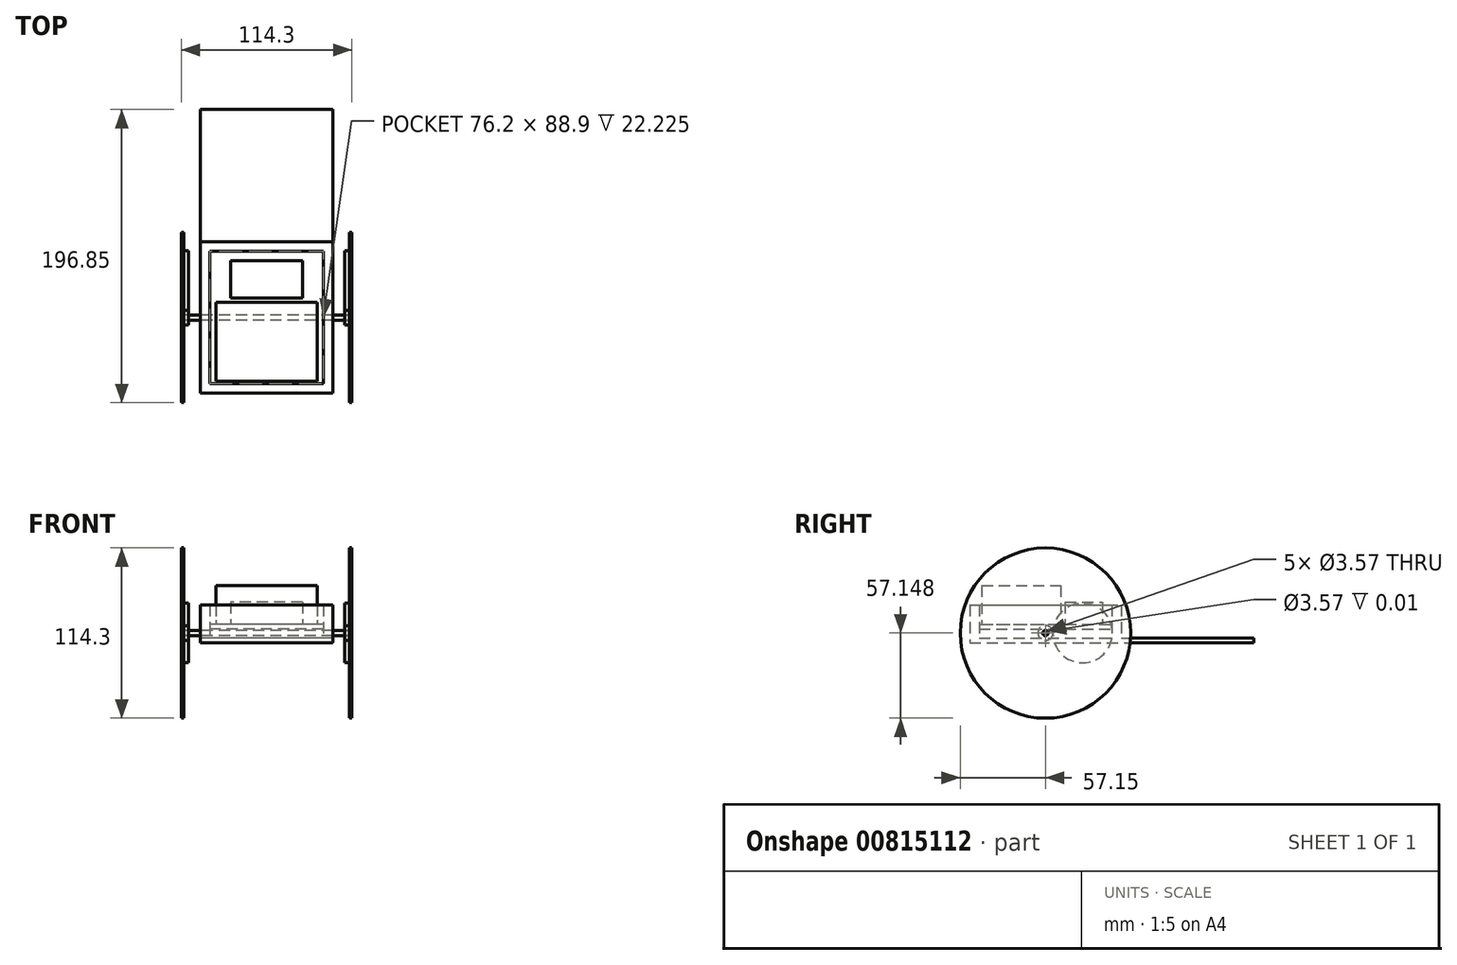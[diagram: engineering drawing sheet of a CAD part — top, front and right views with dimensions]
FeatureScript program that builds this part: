
annotation { "Feature Type Name" : "Feature", "Feature Type Description" : "" }
export const myFeature = defineFeature(function(context is Context, id is Id, definition is map)
    precondition{}
    {
        {
            var Q0;
            Q0=qCreatedBy(makeId("Top.planeOp"),FACE);
            var sketch = newSketch(context, id + "F0", { "sketchPlane" : qUnion([Q0])});
            skLineSegment(sketch, "E0.bottom", {"start": v(44.45, -50.8) * mm, "end": v(-44.45, -50.8) * mm});
            skLineSegment(sketch, "E0.top", {"start": v(44.45, 50.8) * mm, "end": v(-44.45, 50.8) * mm});
            skLineSegment(sketch, "E0.left", {"start": v(44.45, -50.8) * mm, "end": v(44.45, 50.8) * mm});
            skLineSegment(sketch, "E0.right", {"start": v(-44.45, -50.8) * mm, "end": v(-44.45, 50.8) * mm});
            skPoint(sketch, "E0.middle", {"position": v(0, 0) * mm});
            skLineSegment(sketch, "E1.bottom", {"start": v(38.1, -44.45) * mm, "end": v(-38.1, -44.45) * mm});
            skLineSegment(sketch, "E1.top", {"start": v(38.1, 44.45) * mm, "end": v(-38.1, 44.45) * mm});
            skLineSegment(sketch, "E1.left", {"start": v(38.1, -44.45) * mm, "end": v(38.1, 44.45) * mm});
            skLineSegment(sketch, "E1.right", {"start": v(-38.1, -44.45) * mm, "end": v(-38.1, 44.45) * mm});
            skLineSegment(sketch, "E2.top", {"start": v(-44.45, 139.7) * mm, "end": v(44.45, 139.7) * mm});
            skLineSegment(sketch, "E2.left", {"start": v(-44.45, 50.8) * mm, "end": v(-44.45, 139.7) * mm});
            skLineSegment(sketch, "E2.right", {"start": v(44.45, 50.8) * mm, "end": v(44.45, 139.7) * mm});
            skSolve(sketch);
        }
        {
            var Q0;
            Q0=makeQuery(id+"F0.imprint","IMPRINT",FACE,{"disambiguationData":[TD([[makeQuery(id+"F0.imprint","IMPRINT",EDGE,{"derivedFrom":sQuery(id+"F0.wireOp",EDGE,"E0.bottom")}),-1.0]])]});
            extrude(context, id + "F1", {"entities" : qUnion([Q0]), "depth" : 25.4 * mm, "offsetDistance" : 25.4 * mm});
        }
        {
            var Q0;
            Q0=makeQuery(id+"F0.imprint","IMPRINT",FACE,{"disambiguationData":[TD([[makeQuery(id+"F0.imprint","IMPRINT",EDGE,{"derivedFrom":sQuery(id+"F0.wireOp",EDGE,"E1.bottom")}),-1.0]])]});
            extrude(context, id + "F2", {"entities" : qUnion([Q0]), "operationType" : NewBodyOperationType.ADD, "depth" : 3.17 * mm, "offsetDistance" : 25.4 * mm});
        }
        {
            var Q0;
            Q0=makeQuery(id+"F1.opExtrude","SWEPT_FACE",FACE,{"disambiguationData":[OSD([sQuery(id+"F0.wireOp",EDGE,"E1.right")])]});
            var sketch = newSketch(context, id + "F3", { "sketchPlane" : qUnion([Q0])});
            skLineSegment(sketch, "E3.bottom", {"start": v(-44.45, 12.3) * mm, "end": v(44.45, 12.3) * mm});
            skLineSegment(sketch, "E3.top", {"start": v(-44.45, 9.13) * mm, "end": v(44.45, 9.13) * mm});
            skLineSegment(sketch, "E3.left", {"start": v(-44.45, 12.3) * mm, "end": v(-44.45, 9.13) * mm});
            skLineSegment(sketch, "E3.right", {"start": v(44.45, 12.3) * mm, "end": v(44.45, 9.13) * mm});
            skSolve(sketch);
        }
        {
            var Q0;
            Q0=makeQuery(id+"F3.imprint","IMPRINT",FACE,{"disambiguationData":[TD([[makeQuery(id+"F3.imprint","IMPRINT",EDGE,{"derivedFrom":sQuery(id+"F3.wireOp",EDGE,"E3.bottom")}),-1.0]])]});
            extrude(context, id + "F4", {"entities" : qUnion([Q0]), "depth" : 76.2 * mm, "offsetDistance" : 25.4 * mm});
        }
        {
            var Q0;
            Q0=makeQuery(id+"F4.opExtrude","SWEPT_FACE",FACE,{"disambiguationData":[OSD([sQuery(id+"F3.wireOp",EDGE,"E3.bottom")])]});
            var sketch = newSketch(context, id + "F5", { "sketchPlane" : qUnion([Q0])});
            skLineSegment(sketch, "E4.bottom", {"start": v(24, 13.2) * mm, "end": v(-24, 13.2) * mm});
            skLineSegment(sketch, "E4.top", {"start": v(24, 38.2) * mm, "end": v(-24, 38.2) * mm});
            skLineSegment(sketch, "E4.left", {"start": v(24, 13.2) * mm, "end": v(24, 38.2) * mm});
            skLineSegment(sketch, "E4.right", {"start": v(-24, 13.2) * mm, "end": v(-24, 38.2) * mm});
            skPoint(sketch, "E4.middle", {"position": v(0, 25.7) * mm});
            skLineSegment(sketch, "E5.bottom", {"start": v(34, -42.7) * mm, "end": v(-34, -42.7) * mm});
            skLineSegment(sketch, "E5.top", {"start": v(34, 10.3) * mm, "end": v(-34, 10.3) * mm});
            skLineSegment(sketch, "E5.left", {"start": v(34, -42.7) * mm, "end": v(34, 10.3) * mm});
            skLineSegment(sketch, "E5.right", {"start": v(-34, -42.7) * mm, "end": v(-34, 10.3) * mm});
            skPoint(sketch, "E5.middle", {"position": v(0, -16.2) * mm});
            skSolve(sketch);
        }
        {
            var Q0;
            Q0=makeQuery(id+"F5.imprint","IMPRINT",FACE,{"disambiguationData":[TD([[makeQuery(id+"F5.imprint","IMPRINT",EDGE,{"derivedFrom":sQuery(id+"F5.wireOp",EDGE,"E4.bottom")}),-1.0]])]});
            extrude(context, id + "F6", {"entities" : qUnion([Q0]), "depth" : 15 * mm, "offsetDistance" : 25.4 * mm});
        }
        {
            var Q0;
            {var subQ0=sQuery(id+"F5.wireOp",EDGE,"E5.top");Q0=makeQuery(id+"F5.imprint","IMPRINT",FACE,{"disambiguationData":[TD([[makeQuery(id+"F5.imprint","IMPRINT",EDGE,{"derivedFrom":subQ0}),1.0]])]});}
            extrude(context, id + "F7", {"entities" : qUnion([Q0]), "depth" : 26 * mm, "offsetDistance" : 25.4 * mm});
        }
        {
            var Q0;
            Q0=makeQuery(id+"F1.opExtrude","SWEPT_FACE",FACE,{"disambiguationData":[OSD([sQuery(id+"F0.wireOp",EDGE,"E0.right")])]});
            var sketch = newSketch(context, id + "F8", { "sketchPlane" : qUnion([Q0])});
            skLineSegment(sketch, "E6", {"start": v(0, 0) * mm, "end": v(0, 25.4) * mm, "construction": true});
            skCircle(sketch, "E7", {"center": v(0, 6.55) * mm, "radius": 1.79 * mm});
            skSolve(sketch);
        }
        {
            var Q0;
            Q0=makeQuery(id+"F8.imprint","IMPRINT",FACE,{"disambiguationData":[TD([[makeQuery(id+"F8.imprint","IMPRINT",EDGE,{"derivedFrom":sQuery(id+"F8.wireOp",EDGE,"E7")}),1.0]])]});
            extrude(context, id + "F9", {"entities" : qUnion([Q0]), "operationType" : NewBodyOperationType.REMOVE, "oppositeDirection" : true, "depth" : 6.35 * mm, "offsetDistance" : 25.4 * mm});
        }
        {
            var Q0;
            Q0=makeQuery(id+"F1.opExtrude","SWEPT_FACE",FACE,{"disambiguationData":[OSD([sQuery(id+"F0.wireOp",EDGE,"E0.left")])]});
            var sketch = newSketch(context, id + "F10", { "sketchPlane" : qUnion([Q0])});
            skLineSegment(sketch, "E8", {"start": v(0, 0) * mm, "end": v(0, 25.4) * mm, "construction": true});
            skCircle(sketch, "E9", {"center": v(0, 6.55) * mm, "radius": 1.79 * mm});
            skSolve(sketch);
        }
        {
            var Q0;
            Q0=makeQuery(id+"F10.imprint","IMPRINT",FACE,{"disambiguationData":[TD([[makeQuery(id+"F10.imprint","IMPRINT",EDGE,{"derivedFrom":sQuery(id+"F10.wireOp",EDGE,"E9")}),1.0]])]});
            extrude(context, id + "F11", {"entities" : qUnion([Q0]), "operationType" : NewBodyOperationType.REMOVE, "oppositeDirection" : true, "depth" : 1 / 101.6 * mm, "offsetDistance" : 25.4 * mm});
        }
        {
            var Q0;
            Q0=makeQuery(id+"F8.imprint","IMPRINT",FACE,{"disambiguationData":[TD([[makeQuery(id+"F8.imprint","IMPRINT",EDGE,{"derivedFrom":sQuery(id+"F8.wireOp",EDGE,"E7")}),1.0]])]});
            extrude(context, id + "F12", {"entities" : qUnion([Q0]), "oppositeDirection" : true, "depth" : 57.15 * mm, "offsetDistance" : 25.4 * mm, "hasSecondDirection" : true, "secondDirectionOppositeDirection" : false, "secondDirectionDepth" : 57.15 * mm});
        }
        {
            var Q0;
            Q0=makeQuery(id+"F12.opExtrude","SWEPT_BODY",BODY,{"disambiguationData":[OSD([sQuery(id+"F8.wireOp",EDGE,"E7")])]});
            transform(context, id + "F13", {"entities" : qUnion([Q0]), "transformType" : TransformType.TRANSLATION_3D, "dx" : 38.1 * mm, "dy" : 0 * mm, "dz" : 0 * mm, "makeCopy" : false});
        }
        {
            var Q0;
            Q0=makeQuery(id+"F12.opExtrude","SWEPT_BODY",BODY,{"disambiguationData":[OSD([sQuery(id+"F8.wireOp",EDGE,"E7")])]});
            transform(context, id + "F14", {"entities" : qUnion([Q0]), "transformType" : TransformType.TRANSLATION_3D, "dx" : 6.35 * mm, "dy" : 0 * mm, "dz" : 0 * mm, "makeCopy" : false});
        }
        {
            var Q0;
            Q0=makeQuery(id+"F12.opExtrude","CAP_FACE",FACE,{"disambiguationData":[OSD([sQuery(id+"F8.wireOp",EDGE,"E7")])],"isStart":false});
            var sketch = newSketch(context, id + "F15", { "sketchPlane" : qUnion([Q0])});
            skCircle(sketch, "E10", {"center": v(0, 6.55) * mm, "radius": 57.15 * mm});
            skSolve(sketch);
        }
        {
            var Q0;
            Q0=makeQuery(id+"F15.imprint","IMPRINT",FACE,{"disambiguationData":[TD([[makeQuery(id+"F15.imprint","IMPRINT",EDGE,{"derivedFrom":sQuery(id+"F15.wireOp",EDGE,"E10")}),1.0]])]});
            extrude(context, id + "F16", {"entities" : qUnion([Q0]), "oppositeDirection" : true, "depth" : 1.59 * mm, "offsetDistance" : 25.4 * mm});
        }
        {
            var Q0;
            Q0=makeQuery(id+"F12.opExtrude","CAP_FACE",FACE,{"disambiguationData":[OSD([sQuery(id+"F8.wireOp",EDGE,"E7")])],"isStart":true});
            var sketch = newSketch(context, id + "F17", { "sketchPlane" : qUnion([Q0])});
            skCircle(sketch, "E11", {"center": v(0, 6.55) * mm, "radius": 57.15 * mm});
            skSolve(sketch);
        }
        {
            var Q0;
            Q0=makeQuery(id+"F17.imprint","IMPRINT",FACE,{"disambiguationData":[TD([[makeQuery(id+"F17.imprint","IMPRINT",EDGE,{"derivedFrom":sQuery(id+"F17.wireOp",EDGE,"E11")}),1.0]])]});
            extrude(context, id + "F18", {"entities" : qUnion([Q0]), "oppositeDirection" : true, "depth" : 1.59 * mm, "offsetDistance" : 25.4 * mm});
        }
        {
            var Q0;
            Q0=makeQuery(id+"F18.opExtrude","CAP_FACE",FACE,{"disambiguationData":[OSD([sQuery(id+"F8.wireOp",EDGE,"E7"),sQuery(id+"F17.wireOp",EDGE,"E11")])],"isStart":false});
            var sketch = newSketch(context, id + "F19", { "sketchPlane" : qUnion([Q0])});
            skSolve(sketch);
        }
        {
            var Q0;
            Q0=makeQuery(id+"F16.opExtrude","CAP_FACE",FACE,{"disambiguationData":[OSD([sQuery(id+"F8.wireOp",EDGE,"E7"),sQuery(id+"F15.wireOp",EDGE,"E10")])],"isStart":false});
            var sketch = newSketch(context, id + "F20", { "sketchPlane" : qUnion([Q0])});
            skCircle(sketch, "E12", {"center": v(0, 6.55) * mm, "radius": 5 * mm});
            skCircle(sketch, "E13", {"center": v(-25, 6.55) * mm, "radius": 20 * mm});
            skSolve(sketch);
        }
        {
            var Q0;
            Q0=makeQuery(id+"F20.imprint","IMPRINT",FACE,{"disambiguationData":[TD([[makeQuery(id+"F20.imprint","IMPRINT",EDGE,{"derivedFrom":sQuery(id+"F20.wireOp",EDGE,"E12")}),1.0]])]});
            extrude(context, id + "F21", {"entities" : qUnion([Q0]), "depth" : 3.17 * mm, "offsetDistance" : 25.4 * mm});
        }
        {
            var Q0;
            Q0=makeQuery(id+"F19.imprint","IMPRINT",FACE,{"disambiguationData":[TD([[makeQuery(id+"F19.imprint","IMPRINT",EDGE,{"derivedFrom":makeQuery(id+"F18.opExtrude","CAP_EDGE",EDGE,{"disambiguationData":[OSD([sQuery(id+"F17.wireOp",EDGE,"E11")])],"isStart":false})}),-1.0]])]});
            var sketch = newSketch(context, id + "F22", { "sketchPlane" : qUnion([Q0])});
            skCircle(sketch, "E14", {"center": v(0, 6.55) * mm, "radius": 5 * mm});
            skCircle(sketch, "E15", {"center": v(25, 6.55) * mm, "radius": 20 * mm});
            skSolve(sketch);
        }
        {
            var Q0;
            Q0=makeQuery(id+"F22.imprint","IMPRINT",FACE,{"disambiguationData":[TD([[makeQuery(id+"F22.imprint","IMPRINT",EDGE,{"derivedFrom":sQuery(id+"F22.wireOp",EDGE,"E14")}),1.0]])]});
            extrude(context, id + "F23", {"entities" : qUnion([Q0]), "depth" : 3.17 * mm, "offsetDistance" : 25.4 * mm});
        }
        {
            var Q0;
            Q0=makeQuery(id+"F20.imprint","IMPRINT",FACE,{"disambiguationData":[TD([[makeQuery(id+"F20.imprint","IMPRINT",EDGE,{"derivedFrom":sQuery(id+"F20.wireOp",EDGE,"E13")}),1.0]])]});
            extrude(context, id + "F24", {"entities" : qUnion([Q0]), "depth" : 3.17 * mm, "offsetDistance" : 25.4 * mm});
        }
        {
            var Q0;
            Q0=makeQuery(id+"F22.imprint","IMPRINT",FACE,{"disambiguationData":[TD([[makeQuery(id+"F22.imprint","IMPRINT",EDGE,{"derivedFrom":sQuery(id+"F22.wireOp",EDGE,"E15")}),1.0]])]});
            extrude(context, id + "F25", {"entities" : qUnion([Q0]), "depth" : 3.17 * mm, "offsetDistance" : 25.4 * mm});
        }
        {
            var Q0;
            Q0=makeQuery(id+"F0.imprint","IMPRINT",FACE,{"disambiguationData":[TD([[makeQuery(id+"F0.imprint","IMPRINT",EDGE,{"derivedFrom":sQuery(id+"F0.wireOp",EDGE,"E0.top")}),-1.0]])]});
            extrude(context, id + "F26", {"entities" : qUnion([Q0]), "operationType" : NewBodyOperationType.ADD, "depth" : 3.17 * mm, "offsetDistance" : 25.4 * mm});
        }
    });
